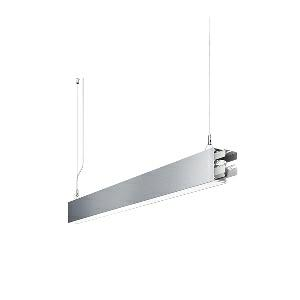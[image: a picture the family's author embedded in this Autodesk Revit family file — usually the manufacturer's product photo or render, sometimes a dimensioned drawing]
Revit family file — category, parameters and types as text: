
# Revit family: dotoo_line_-_dlp_1000_830_d_sta_00805840_1ce5
name_source: partatom
category: Lighting Fixtures
units: mm (PartAtom-declared; Revit-internal decimal feet)

## family parameters
Cut with Voids When Loaded = No
Host = Face
Light Source = No
Part Type = Normal
Room Calculation Point = No
Round Connector Dimension = Use Diameter
Shared = No

## types (1)
- DOTOO.line - DLP 1000/830/D STA (1 x LED, 1000 lm, 3000K)
    Apparent Load = 10 VA
    Approval mark = CE
    CIE Flux Codes = 67 91 98 100 100
    Color Rendering = 80-89
    Color Temperature = 3000K
    Control Gear = Electronic ballast
    Default Elevation = 1800 mm
    Description = DLP 1000/830/D|Suspended luminaire|light source: LED|connected load: 220-240 V, 50/60 Hz|Power consumption: approx. 10 W|standby: approx. 0,20|luminous flux: 1000 lm|luminous efficacy: 100 lm/W|light distribution: Direct|direct ratio: approx. 100 %|colour temperature: Warm white, ca. 3000 K|color rendering index (CRI): >= 80|chromaticity tolerance:  3 SDCM|System of protection: IP 40|technology: Continuously dimmable|luminaire body|material: Sectional aluminium|colour: Silver|lamp cover: Acrylic (PMMA), Clear|mains lead: 2.00 m With free stranded wires|Fastening: Steel cable 0.3 - 0.7 m|glare control: Prism aperture|luminance(L65): <= 3000 cd/m|unified glare rating(4H 8H): <=  19|special features: DALI Load 1x, TouchDIM - dimming via standard switch, Through-wired, up to 18 m on one mains connection, Flicker-free, Suitable as emergency lighting, Start luminaire with mains connection, Mechanical and electrical connection of the individual modules without tools|
    Frequency = 50 Hz
    Height = 110 mm
    Lamp = 1 x LED
    Lamp Light Flux = 1000 lm
    Lamp count = 1
    Length = 848 mm
    Luminous efficacy = 100 lm/W
    Manufacturer = Waldmann
    ModVariant = No
    Model = 00805840
    Mounting Place = Ceiling
    Mounting Type = Pendant
    Number of Poles = 1
    OnlyDefault = Yes
    Power Factor = 1
    Product Name = DOTOO.line - DLP 1000/830/D STA
    Product group = Suspended luminaire
    ProductGroupID = 9
    Protection Class = Protection class I
    Protection Degree = IP 40
    RLX_Detail_Level = 1
    RLX_Emergency_Light_Flux = 0 lm
    RLX_Emergency_Type = 0
    RLX_Emergency_Type_DB = No
    RlxData = <blob elided: 20989 chars, md5=ba45a30b>
    Socket = socket
    Standby Power = 0 W
    System Light Flux = 1000 lm
    System Power = 10 W
    Type Comments = Product without accessories
    Type Image = 113298000-00692558.jpg
    URL = http://relux.com
    VarID = ---
    Voltage = 230 V
    Voltage Range = 220-240 V
    Weight = 0.00 kg
    Width = 60 mm  [stored 0.19685 ft]

note: [stored X ft] marks values corroborated as IEEE doubles in the binary element streams (Revit-internal decimal feet)

## geometry (parser evidence)
native form markers: Blend x4, Sweep x13
no freeform markers — native parametric forms only
